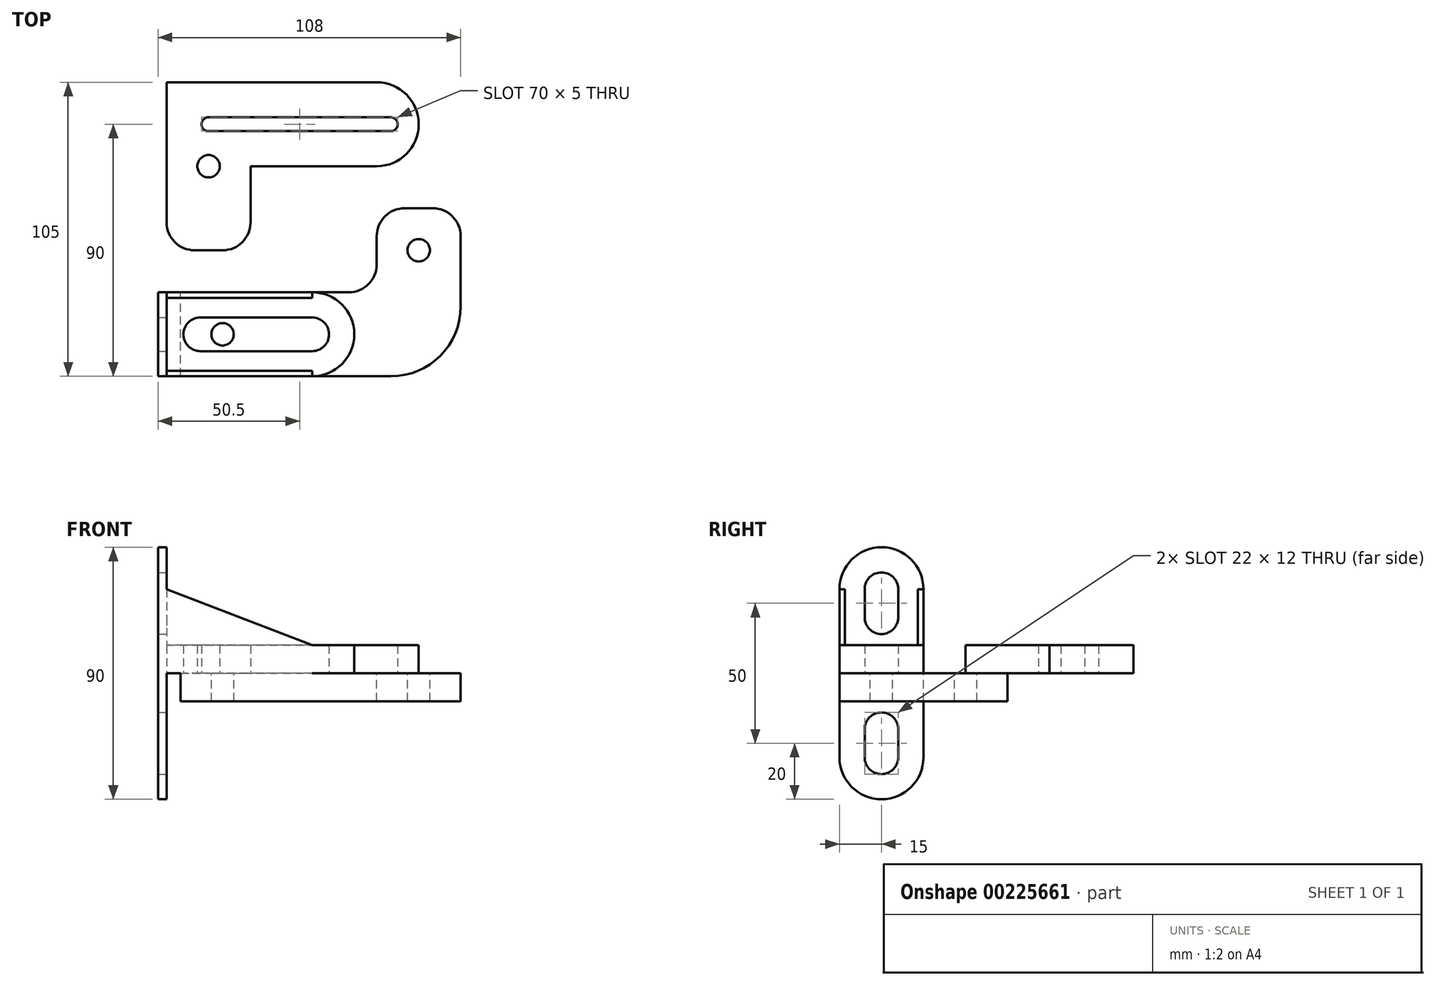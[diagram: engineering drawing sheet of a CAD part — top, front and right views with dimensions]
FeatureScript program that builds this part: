
annotation { "Feature Type Name" : "Feature", "Feature Type Description" : "" }
export const myFeature = defineFeature(function(context is Context, id is Id, definition is map)
    precondition{}
    {
        {
            var Q0;
            Q0=qCreatedBy(makeId("Top.planeOp"),FACE);
            var sketch = newSketch(context, id + "F0", { "sketchPlane" : qUnion([Q0])});
            skLineSegment(sketch, "E0", {"start": v(0, 15) * mm, "end": v(0, -15) * mm});
            skLineSegment(sketch, "E1", {"start": v(0, -15) * mm, "end": v(52, -15) * mm});
            skLineSegment(sketch, "E2", {"start": v(0, 15) * mm, "end": v(52, 15) * mm});
            skArc(sketch, "E3", {"start": v(52, -15) * mm, "mid": v(67, 0) * mm, "end": v(52, 15) * mm});
            skLineSegment(sketch, "E4", {"start": v(52, 0) * mm, "end": v(12, 0) * mm});
            skArc(sketch, "E5.0.startCap", {"start": v(52, 6) * mm, "mid": v(58, 0) * mm, "end": v(52, -6) * mm});
            skArc(sketch, "E5.0.endCap", {"start": v(12, -6) * mm, "mid": v(6, 0) * mm, "end": v(12, 6) * mm});
            skLineSegment(sketch, "E5.0.left", {"start": v(52, -6) * mm, "end": v(12, -6) * mm});
            skLineSegment(sketch, "E5.0.right", {"start": v(52, 6) * mm, "end": v(12, 6) * mm});
            skLineSegment(sketch, "E6.0", {"start": v(0, -13) * mm, "end": v(52, -13) * mm});
            skArc(sketch, "E6.1", {"start": v(52, -13) * mm, "mid": v(65, 0) * mm, "end": v(52, 13) * mm});
            skLineSegment(sketch, "E6.2", {"start": v(0, 13) * mm, "end": v(52, 13) * mm});
            skSolve(sketch);
        }
        {
            var Q0;
            Q0 = qSketchRegion(id + "F0", true);
            extrude(context, id + "F1", {"entities" : qUnion([Q0]), "depth" : 10 * mm});
        }
        {
            var Q0;
            Q0=qCreatedBy(makeId("Right.planeOp"),FACE);
            var sketch = newSketch(context, id + "F2", { "sketchPlane" : qUnion([Q0])});
            skLineSegment(sketch, "E7", {"start": v(-15, 0) * mm, "end": v(-15, 30) * mm});
            skLineSegment(sketch, "E8", {"start": v(-15, 0) * mm, "end": v(-15, -30) * mm});
            skLineSegment(sketch, "E9", {"start": v(15, 0) * mm, "end": v(15, 30) * mm});
            skLineSegment(sketch, "E10", {"start": v(15, 0) * mm, "end": v(15, -30) * mm});
            skArc(sketch, "E11", {"start": v(-15, -30) * mm, "mid": v(0, -45) * mm, "end": v(15, -30) * mm});
            skArc(sketch, "E12", {"start": v(15, 30) * mm, "mid": v(0, 45) * mm, "end": v(-15, 30) * mm});
            skLineSegment(sketch, "E13", {"start": v(0, 30) * mm, "end": v(0, 20) * mm});
            skLineSegment(sketch, "E14", {"start": v(0, -30) * mm, "end": v(0, -20) * mm});
            skArc(sketch, "E15.0.startCap", {"start": v(6, -30) * mm, "mid": v(0, -36) * mm, "end": v(-6, -30) * mm});
            skArc(sketch, "E15.0.endCap", {"start": v(-6, -20) * mm, "mid": v(0, -14) * mm, "end": v(6, -20) * mm});
            skLineSegment(sketch, "E15.0.left", {"start": v(-6, -30) * mm, "end": v(-6, -20) * mm});
            skLineSegment(sketch, "E15.0.right", {"start": v(6, -30) * mm, "end": v(6, -20) * mm});
            skArc(sketch, "E16.0.startCap", {"start": v(-6, 30) * mm, "mid": v(0, 36) * mm, "end": v(6, 30) * mm});
            skArc(sketch, "E16.0.endCap", {"start": v(6, 20) * mm, "mid": v(0, 14) * mm, "end": v(-6, 20) * mm});
            skLineSegment(sketch, "E16.0.left", {"start": v(6, 30) * mm, "end": v(6, 20) * mm});
            skLineSegment(sketch, "E16.0.right", {"start": v(-6, 30) * mm, "end": v(-6, 20) * mm});
            skSolve(sketch);
        }
        {
            var Q0;
            Q0 = qSketchRegion(id + "F2", true);
            extrude(context, id + "F3", {"entities" : qUnion([Q0]), "operationType" : NewBodyOperationType.ADD, "oppositeDirection" : true, "depth" : 3 * mm});
        }
        {
            var Q0;
            Q0=makeQuery(id+"F1.opExtrude","CAP_FACE",FACE,{"disambiguationData":[OSD([sQuery(id+"F0.wireOp",EDGE,"E0"),sQuery(id+"F0.wireOp",EDGE,"E1"),sQuery(id+"F0.wireOp",EDGE,"E2"),sQuery(id+"F0.wireOp",EDGE,"E3"),sQuery(id+"F0.wireOp",EDGE,"E5.0.startCap"),sQuery(id+"F0.wireOp",EDGE,"E5.0.endCap"),sQuery(id+"F0.wireOp",EDGE,"E5.0.left"),sQuery(id+"F0.wireOp",EDGE,"E5.0.right")])],"isStart":true});
            var sketch = newSketch(context, id + "F4", { "sketchPlane" : qUnion([Q0])});
            skLineSegment(sketch, "E17", {"start": v(5, 15) * mm, "end": v(5, -15) * mm});
            skLineSegment(sketch, "E18", {"start": v(5, -15) * mm, "end": v(75, -15) * mm});
            skLineSegment(sketch, "E19", {"start": v(75, -15) * mm, "end": v(75, -45) * mm});
            skLineSegment(sketch, "E20", {"start": v(75, -45) * mm, "end": v(105, -45) * mm});
            skLineSegment(sketch, "E21", {"start": v(105, -45) * mm, "end": v(105, 15) * mm});
            skLineSegment(sketch, "E22", {"start": v(105, 15) * mm, "end": v(5, 15) * mm});
            skCircle(sketch, "E23", {"center": v(20, 0) * mm, "radius": 4 * mm});
            skPoint(sketch, "E24", {"position": v(90, -30) * mm});
            skPoint(sketch, "E24.positionSnap0", {"position": v(90, -45) * mm});
            skCircle(sketch, "E25", {"center": v(90, -30) * mm, "radius": 4 * mm});
            skSolve(sketch);
        }
        {
            var Q0;
            {var subQ3=sQuery(id+"F4.wireOp",EDGE,"E17");Q0=makeQuery(id+"F4.imprint","IMPRINT",FACE,{"disambiguationData":[TD([[makeQuery(id+"F4.imprint","IMPRINT",EDGE,{"derivedFrom":subQ3}),1.0]])]});}
            var Q1;
            {var subQ3=sQuery(id+"F4.wireOp",EDGE,"E19");Q1=makeQuery(id+"F4.imprint","IMPRINT",FACE,{"disambiguationData":[TD([[makeQuery(id+"F4.imprint","IMPRINT",EDGE,{"derivedFrom":subQ3}),1.0]])]});}
            var Q2;
            Q2=makeQuery(id+"F4.imprint","IMPRINT",FACE,{"disambiguationData":[TD([[makeQuery(id+"F4.imprint","IMPRINT",EDGE,{"derivedFrom":sQuery(id+"F4.wireOp",EDGE,"E23")}),-1.0]])]});
            extrude(context, id + "F5", {"entities" : qUnion([Q0, Q1, Q2]), "depth" : 10 * mm});
        }
        {
            var Q0;
            Q0=makeQuery(id+"F5.opExtrude","SWEPT_EDGE",EDGE,{"disambiguationData":[OSD([sQuery(id+"F4.wireOp",EDGE,"E21"),sQuery(id+"F4.wireOp",EDGE,"E22")])]});
            fillet(context, id + "F6", {"entities" : qUnion([Q0]), "radius" : 25 * mm, "tangentPropagation" : true, "allowEdgeOverflow" : false});
        }
        {
            var Q0;
            Q0=makeQuery(id+"F5.opExtrude","SWEPT_EDGE",EDGE,{"disambiguationData":[OSD([sQuery(id+"F4.wireOp",EDGE,"E19"),sQuery(id+"F4.wireOp",EDGE,"E20")])]});
            var Q1;
            Q1=makeQuery(id+"F5.opExtrude","SWEPT_EDGE",EDGE,{"disambiguationData":[OSD([sQuery(id+"F4.wireOp",EDGE,"E20"),sQuery(id+"F4.wireOp",EDGE,"E21")])]});
            var Q2;
            Q2=makeQuery(id+"F5.opExtrude","SWEPT_EDGE",EDGE,{"disambiguationData":[OSD([sQuery(id+"F0.wireOp",EDGE,"E2"),sQuery(id+"F4.wireOp",EDGE,"E18"),sQuery(id+"F4.wireOp",EDGE,"E19")])]});
            fillet(context, id + "F7", {"entities" : qUnion([Q0, Q1, Q2]), "radius" : 10 * mm, "tangentPropagation" : true, "allowEdgeOverflow" : false});
        }
        {
            var Q0;
            {var subQ1=sQuery(id+"F0.wireOp",EDGE,"E1");Q0=makeQuery(id+"F0.imprint","IMPRINT",FACE,{"disambiguationData":[TD([[makeQuery(id+"F0.imprint","IMPRINT",EDGE,{"derivedFrom":subQ1}),1.0]])]});}
            extrude(context, id + "F8", {"entities" : qUnion([Q0]), "operationType" : NewBodyOperationType.ADD, "depth" : 30 * mm});
        }
        {
            var Q0;
            {var subQ0=sQuery(id+"F0.wireOp",EDGE,"E1");Q0=makeQuery(id+"F8.boolean.opBoolean","MERGE",FACE,{"derivedFrom":[makeQuery(id+"F3.boolean.opBoolean","MERGE",FACE,{"derivedFrom":[makeQuery(id+"F1.opExtrude","SWEPT_FACE",FACE,{"disambiguationData":[OSD([subQ0])]}),makeQuery(id+"F3.opExtrude","SWEPT_FACE",FACE,{"disambiguationData":[OSD([sQuery(id+"F2.wireOp",EDGE,"E7"),sQuery(id+"F2.wireOp",EDGE,"E8")])]})]}),makeQuery(id+"F8.opExtrude","SWEPT_FACE",FACE,{"disambiguationData":[OSD([subQ0])]})]});}
            var sketch = newSketch(context, id + "F9", { "sketchPlane" : qUnion([Q0])});
            skLineSegment(sketch, "E26", {"start": v(0, 30) * mm, "end": v(52, 10) * mm});
            skLineSegment(sketch, "E27", {"start": v(52, 10) * mm, "end": v(75.37, 10) * mm});
            skLineSegment(sketch, "E28", {"start": v(75.37, 10) * mm, "end": v(75.37, 30) * mm});
            skLineSegment(sketch, "E29", {"start": v(75.37, 30) * mm, "end": v(0, 30) * mm});
            skSolve(sketch);
        }
        {
            var Q0;
            {var subQ0=sQuery(id+"F9.wireOp",EDGE,"E27");Q0=makeQuery(id+"F9.imprint","IMPRINT",FACE,{"disambiguationData":[TD([[makeQuery(id+"F9.imprint","IMPRINT",EDGE,{"derivedFrom":subQ0}),1.0]])]});}
            var Q1;
            {var subQ0=sQuery(id+"F9.wireOp",EDGE,"E26");Q1=makeQuery(id+"F9.imprint","IMPRINT",FACE,{"disambiguationData":[TD([[makeQuery(id+"F9.imprint","IMPRINT",EDGE,{"derivedFrom":subQ0}),1.0]])]});}
            extrude(context, id + "F10", {"entities" : qUnion([Q0, Q1]), "operationType" : NewBodyOperationType.REMOVE, "oppositeDirection" : true, "depth" : 30 * mm});
        }
        {
            var Q0;
            Q0=makeQuery(id+"F5.opExtrude","SWEPT_FACE",FACE,{"disambiguationData":[OSD([sQuery(id+"F4.wireOp",EDGE,"E21")])]});
            cPlane(context, id + "F11", {"entities" : qUnion([Q0]), "cplaneType" : CPlaneType.OFFSET, "offset" : 15 * mm, "oppositeDirection" : true, "width" : 150 * mm, "height" : 150 * mm});
        }
        {
            var Q0;
            Q0=qCreatedBy(id+"F11.planeOp",FACE);
            var sketch = newSketch(context, id + "F12", { "sketchPlane" : qUnion([Q0])});
            skLineSegment(sketch, "E30", {"start": v(0, 0) * mm, "end": v(30, 0) * mm});
            skLineSegment(sketch, "E31", {"start": v(30, 0) * mm, "end": v(30, 2) * mm});
            skArc(sketch, "E32", {"start": v(30, -8) * mm, "mid": v(40, 2) * mm, "end": v(30, 12) * mm});
            skLineSegment(sketch, "E33", {"start": v(30, -8) * mm, "end": v(30, 12) * mm});
            skSolve(sketch);
        }
        {
            var Q0;
            Q0=qCreatedBy(makeId("Top.planeOp"),FACE);
            var sketch = newSketch(context, id + "F13", { "sketchPlane" : qUnion([Q0])});
            skLineSegment(sketch, "E34", {"start": v(0, 90) * mm, "end": v(90, 90) * mm});
            skLineSegment(sketch, "E35", {"start": v(90, 90) * mm, "end": v(90, 60) * mm});
            skLineSegment(sketch, "E36", {"start": v(90, 60) * mm, "end": v(30, 60) * mm});
            skLineSegment(sketch, "E37", {"start": v(30, 60) * mm, "end": v(30, 30) * mm});
            skLineSegment(sketch, "E38", {"start": v(30, 30) * mm, "end": v(0, 30) * mm});
            skLineSegment(sketch, "E39", {"start": v(0, 30) * mm, "end": v(0, 90) * mm});
            skLineSegment(sketch, "E40", {"start": v(80, 75) * mm, "end": v(15, 75) * mm});
            skPoint(sketch, "E40.startSnap0", {"position": v(90, 75) * mm});
            skArc(sketch, "E41.0.startCap", {"start": v(80, 77.5) * mm, "mid": v(82.5, 75) * mm, "end": v(80, 72.5) * mm});
            skArc(sketch, "E41.0.endCap", {"start": v(15, 72.5) * mm, "mid": v(12.5, 75) * mm, "end": v(15, 77.5) * mm});
            skLineSegment(sketch, "E41.0.left", {"start": v(80, 72.5) * mm, "end": v(15, 72.5) * mm});
            skLineSegment(sketch, "E41.0.right", {"start": v(80, 77.5) * mm, "end": v(15, 77.5) * mm});
            skPoint(sketch, "E42", {"position": v(15, 60) * mm});
            skCircle(sketch, "E43", {"center": v(15, 60) * mm, "radius": 4 * mm});
            skSolve(sketch);
        }
        {
            var Q0;
            Q0 = qSketchRegion(id + "F13", true);
            extrude(context, id + "F14", {"entities" : qUnion([Q0]), "depth" : 10 * mm});
        }
        {
            var Q0;
            Q0=makeQuery(id+"F14.opExtrude","SWEPT_EDGE",EDGE,{"disambiguationData":[OSD([sQuery(id+"F13.wireOp",EDGE,"E35"),sQuery(id+"F13.wireOp",EDGE,"E36")])]});
            var Q1;
            Q1=makeQuery(id+"F14.opExtrude","SWEPT_EDGE",EDGE,{"disambiguationData":[OSD([sQuery(id+"F13.wireOp",EDGE,"E34"),sQuery(id+"F13.wireOp",EDGE,"E35")])]});
            fillet(context, id + "F15", {"entities" : qUnion([Q0, Q1]), "radius" : 15 * mm, "tangentPropagation" : true, "allowEdgeOverflow" : false});
        }
        {
            var Q0;
            Q0=makeQuery(id+"F14.opExtrude","SWEPT_EDGE",EDGE,{"disambiguationData":[OSD([sQuery(id+"F13.wireOp",EDGE,"E38"),sQuery(id+"F13.wireOp",EDGE,"E39")])]});
            var Q1;
            Q1=makeQuery(id+"F14.opExtrude","SWEPT_EDGE",EDGE,{"disambiguationData":[OSD([sQuery(id+"F13.wireOp",EDGE,"E37"),sQuery(id+"F13.wireOp",EDGE,"E38")])]});
            fillet(context, id + "F16", {"entities" : qUnion([Q0, Q1]), "radius" : 10 * mm, "tangentPropagation" : true, "allowEdgeOverflow" : false});
        }
    });
